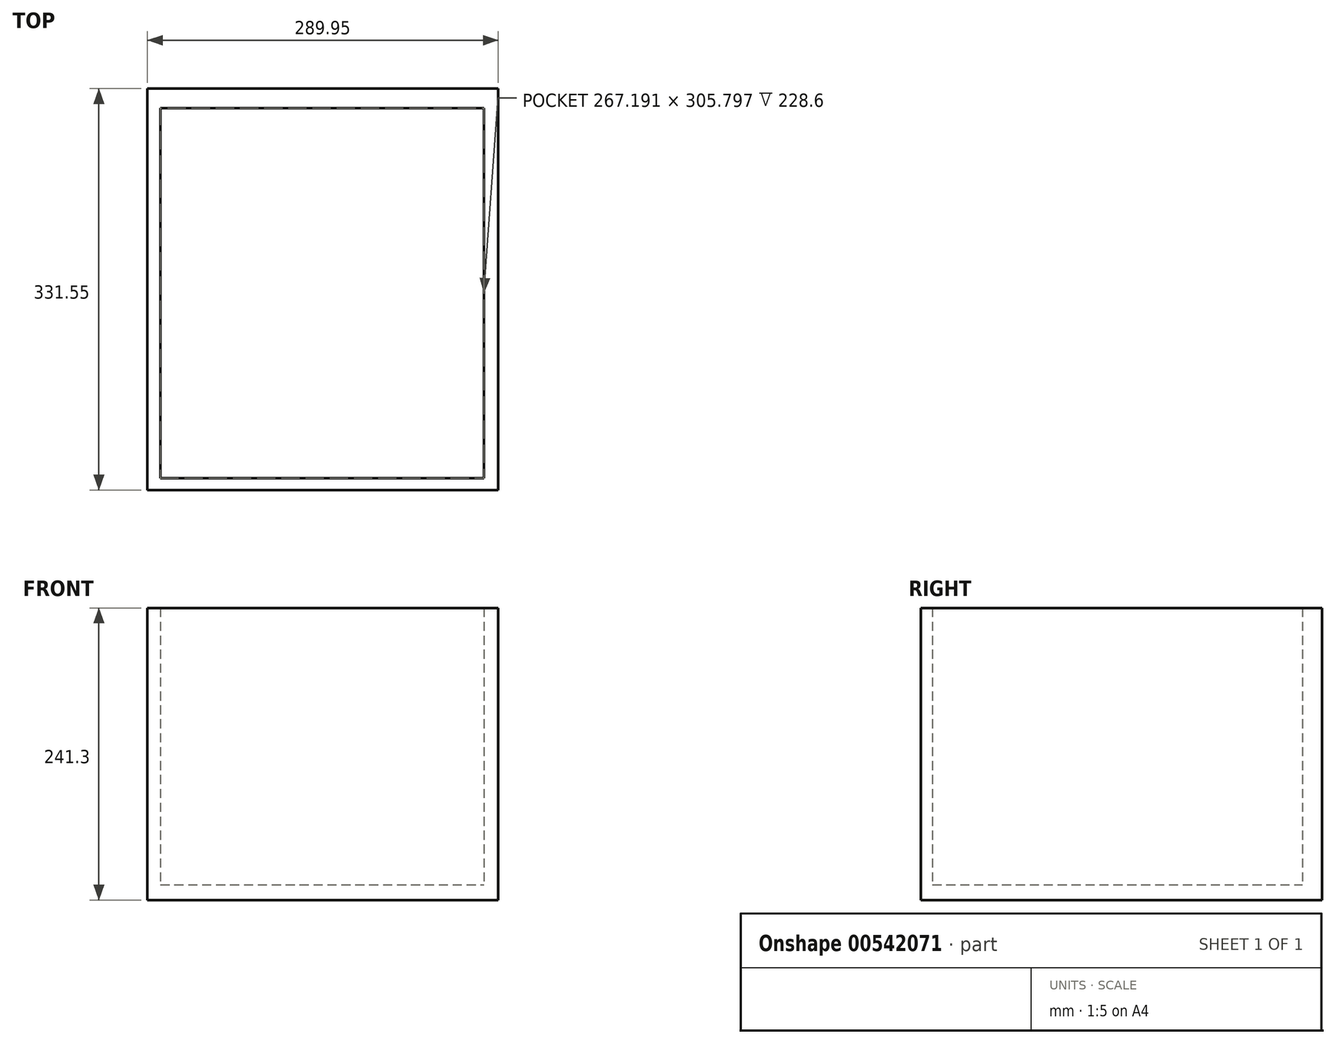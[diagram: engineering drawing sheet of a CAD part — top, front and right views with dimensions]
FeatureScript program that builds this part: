
annotation { "Feature Type Name" : "Feature", "Feature Type Description" : "" }
export const myFeature = defineFeature(function(context is Context, id is Id, definition is map)
    precondition{}
    {
        {
            var Q0;
            Q0=qCreatedBy(makeId("Top.planeOp"),FACE);
            var sketch = newSketch(context, id + "F0", { "sketchPlane" : qUnion([Q0])});
            skLineSegment(sketch, "E0.bottom", {"start": v(-135.36, -205.76) * mm, "end": v(154.6, -205.76) * mm});
            skLineSegment(sketch, "E0.top", {"start": v(-135.36, 125.79) * mm, "end": v(154.6, 125.79) * mm});
            skLineSegment(sketch, "E0.left", {"start": v(-135.36, -205.76) * mm, "end": v(-135.36, 125.79) * mm});
            skLineSegment(sketch, "E0.right", {"start": v(154.6, -205.76) * mm, "end": v(154.6, 125.79) * mm});
            skSolve(sketch);
        }
        {
            var Q0;
            Q0=makeQuery(id+"F0.imprint","IMPRINT",FACE,{"disambiguationData":[TD([[makeQuery(id+"F0.imprint","IMPRINT",EDGE,{"derivedFrom":sQuery(id+"F0.wireOp",EDGE,"E0.bottom")}),1.0]])]});
            extrude(context, id + "F1", {"entities" : qUnion([Q0]), "depth" : 12.7 * mm, "offsetDistance" : 25.4 * mm});
        }
        {
            var Q0;
            Q0=makeQuery(id+"F1.opExtrude","CAP_FACE",FACE,{"disambiguationData":[OSD([sQuery(id+"F0.wireOp",EDGE,"E0.bottom"),sQuery(id+"F0.wireOp",EDGE,"E0.top"),sQuery(id+"F0.wireOp",EDGE,"E0.left"),sQuery(id+"F0.wireOp",EDGE,"E0.right")])],"isStart":false});
            var sketch = newSketch(context, id + "F2", { "sketchPlane" : qUnion([Q0])});
            skLineSegment(sketch, "E1.bottom", {"start": v(-124.55, -205.76) * mm, "end": v(-135.36, -205.76) * mm});
            skLineSegment(sketch, "E1.top", {"start": v(-124.55, 125.79) * mm, "end": v(-135.36, 125.79) * mm});
            skLineSegment(sketch, "E1.left", {"start": v(-124.55, -205.76) * mm, "end": v(-124.55, 125.79) * mm});
            skLineSegment(sketch, "E1.right", {"start": v(-135.36, -205.76) * mm, "end": v(-135.36, 125.79) * mm});
            skSolve(sketch);
        }
        {
            var Q0;
            Q0=makeQuery(id+"F2.imprint","IMPRINT",FACE,{"disambiguationData":[TD([[makeQuery(id+"F2.imprint","IMPRINT",EDGE,{"derivedFrom":sQuery(id+"F2.wireOp",EDGE,"E1.bottom")}),1.0]])]});
            extrude(context, id + "F3", {"entities" : qUnion([Q0]), "operationType" : NewBodyOperationType.ADD, "depth" : 228.6 * mm, "offsetDistance" : 25.4 * mm});
        }
        {
            var Q0;
            Q0=makeQuery(id+"F1.opExtrude","CAP_FACE",FACE,{"disambiguationData":[OSD([sQuery(id+"F0.wireOp",EDGE,"E0.bottom"),sQuery(id+"F0.wireOp",EDGE,"E0.top"),sQuery(id+"F0.wireOp",EDGE,"E0.left"),sQuery(id+"F0.wireOp",EDGE,"E0.right")])],"isStart":false});
            var sketch = newSketch(context, id + "F4", { "sketchPlane" : qUnion([Q0])});
            skLineSegment(sketch, "E2.bottom", {"start": v(154.6, 109.74) * mm, "end": v(-124.55, 109.74) * mm});
            skLineSegment(sketch, "E2.top", {"start": v(154.6, 125.79) * mm, "end": v(-124.55, 125.79) * mm});
            skLineSegment(sketch, "E2.left", {"start": v(154.6, 109.74) * mm, "end": v(154.6, 125.79) * mm});
            skLineSegment(sketch, "E2.right", {"start": v(-124.55, 109.74) * mm, "end": v(-124.55, 125.79) * mm});
            skSolve(sketch);
        }
        {
            var Q0;
            Q0=makeQuery(id+"F4.imprint","IMPRINT",FACE,{"disambiguationData":[TD([[makeQuery(id+"F4.imprint","IMPRINT",EDGE,{"derivedFrom":sQuery(id+"F4.wireOp",EDGE,"E2.bottom")}),-1.0]])]});
            extrude(context, id + "F5", {"entities" : qUnion([Q0]), "operationType" : NewBodyOperationType.ADD, "depth" : 228.6 * mm, "offsetDistance" : 25.4 * mm});
        }
        {
            var Q0;
            Q0=makeQuery(id+"F1.opExtrude","CAP_FACE",FACE,{"disambiguationData":[OSD([sQuery(id+"F0.wireOp",EDGE,"E0.bottom"),sQuery(id+"F0.wireOp",EDGE,"E0.top"),sQuery(id+"F0.wireOp",EDGE,"E0.left"),sQuery(id+"F0.wireOp",EDGE,"E0.right")])],"isStart":false});
            var sketch = newSketch(context, id + "F6", { "sketchPlane" : qUnion([Q0])});
            skLineSegment(sketch, "E3.bottom", {"start": v(142.64, -205.76) * mm, "end": v(154.6, -205.76) * mm});
            skLineSegment(sketch, "E3.top", {"start": v(142.64, 109.74) * mm, "end": v(154.6, 109.74) * mm});
            skLineSegment(sketch, "E3.left", {"start": v(142.64, -205.76) * mm, "end": v(142.64, 109.74) * mm});
            skLineSegment(sketch, "E3.right", {"start": v(154.6, -205.76) * mm, "end": v(154.6, 109.74) * mm});
            skSolve(sketch);
        }
        {
            var Q0;
            Q0=makeQuery(id+"F6.imprint","IMPRINT",FACE,{"disambiguationData":[TD([[makeQuery(id+"F6.imprint","IMPRINT",EDGE,{"derivedFrom":sQuery(id+"F6.wireOp",EDGE,"E3.bottom")}),1.0]])]});
            extrude(context, id + "F7", {"entities" : qUnion([Q0]), "operationType" : NewBodyOperationType.ADD, "depth" : 228.6 * mm, "offsetDistance" : 25.4 * mm});
        }
        {
            var Q0;
            Q0=makeQuery(id+"F1.opExtrude","CAP_FACE",FACE,{"disambiguationData":[OSD([sQuery(id+"F0.wireOp",EDGE,"E0.bottom"),sQuery(id+"F0.wireOp",EDGE,"E0.top"),sQuery(id+"F0.wireOp",EDGE,"E0.left"),sQuery(id+"F0.wireOp",EDGE,"E0.right")])],"isStart":false});
            var sketch = newSketch(context, id + "F8", { "sketchPlane" : qUnion([Q0])});
            skLineSegment(sketch, "E4.bottom", {"start": v(-124.55, -196.05) * mm, "end": v(152.02, -196.05) * mm});
            skLineSegment(sketch, "E4.top", {"start": v(-124.55, -205.76) * mm, "end": v(152.02, -205.76) * mm});
            skLineSegment(sketch, "E4.left", {"start": v(-124.55, -196.05) * mm, "end": v(-124.55, -205.76) * mm});
            skLineSegment(sketch, "E4.right", {"start": v(152.02, -196.05) * mm, "end": v(152.02, -205.76) * mm});
            skSolve(sketch);
        }
        {
            var Q0;
            {var subQ0=sQuery(id+"F8.wireOp",EDGE,"E4.left");Q0=makeQuery(id+"F8.imprint","IMPRINT",FACE,{"disambiguationData":[TD([[makeQuery(id+"F8.imprint","IMPRINT",EDGE,{"derivedFrom":subQ0}),-1.0]])]});}
            extrude(context, id + "F9", {"entities" : qUnion([Q0]), "operationType" : NewBodyOperationType.ADD, "depth" : 228.6 * mm, "offsetDistance" : 25.4 * mm});
        }
    });
